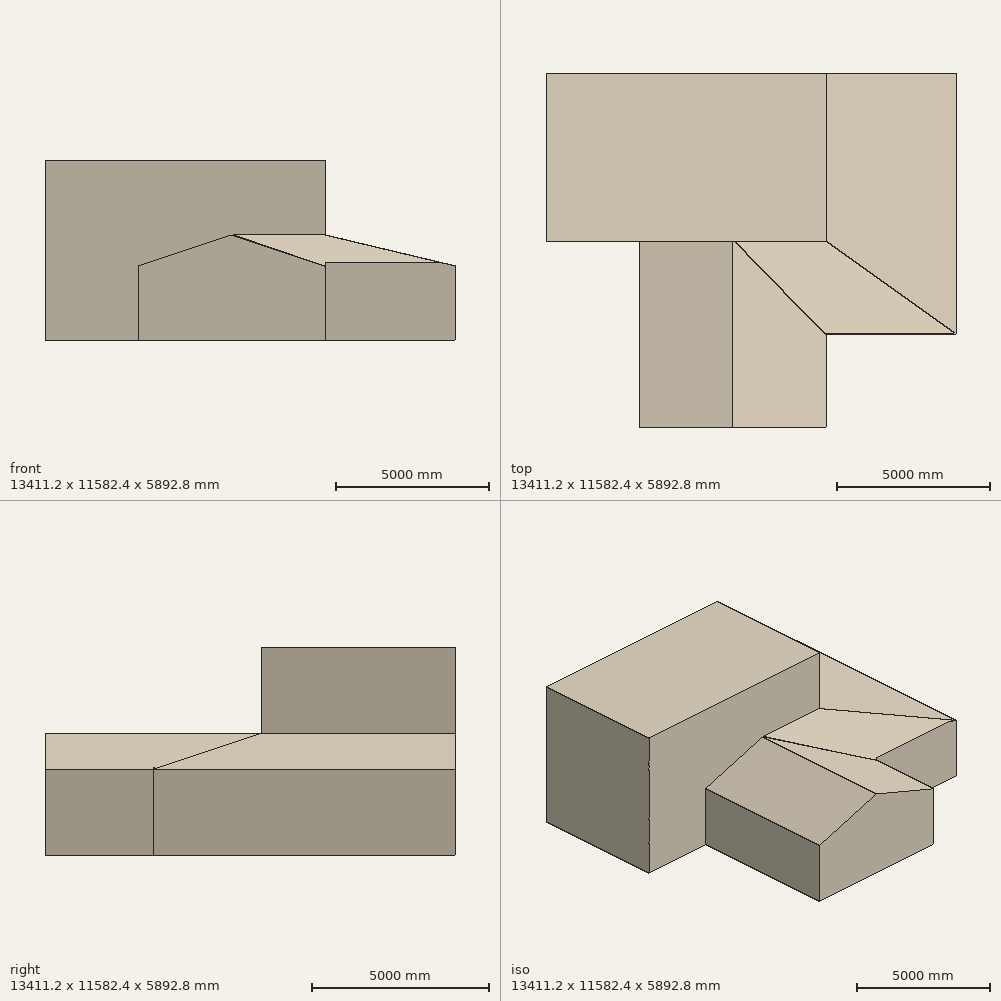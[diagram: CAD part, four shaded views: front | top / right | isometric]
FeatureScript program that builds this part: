
annotation { "Feature Type Name" : "Feature", "Feature Type Description" : "" }
export const myFeature = defineFeature(function(context is Context, id is Id, definition is map)
    precondition{}
    {
        {
            var Q0;
            Q0=qCreatedBy(makeId("Top.planeOp"),FACE);
            var sketch = newSketch(context, id + "F0", { "sketchPlane" : qUnion([Q0])});
            skLineSegment(sketch, "E0.bottom", {"start": v(0, 0) * mm, "end": v(4267.2, 0) * mm});
            skLineSegment(sketch, "E0.top", {"start": v(0, 8534.4) * mm, "end": v(4267.2, 8534.4) * mm});
            skLineSegment(sketch, "E0.left", {"start": v(0, 0) * mm, "end": v(0, 8534.4) * mm});
            skLineSegment(sketch, "E0.right", {"start": v(4267.2, 0) * mm, "end": v(4267.2, 8534.4) * mm});
            skSolve(sketch);
        }
        {
            var Q0;
            Q0=makeQuery(id+"F0.imprint","IMPRINT",FACE,{"disambiguationData":[TD([[makeQuery(id+"F0.imprint","IMPRINT",EDGE,{"derivedFrom":sQuery(id+"F0.wireOp",EDGE,"E0.bottom")}),1.0]])]});
            extrude(context, id + "F1", {"entities" : qUnion([Q0]), "depth" : 3454.4 * mm});
        }
        {
            var Q0;
            Q0=makeQuery(id+"F1.opExtrude","SWEPT_FACE",FACE,{"disambiguationData":[OSD([sQuery(id+"F0.wireOp",EDGE,"E0.bottom")])]});
            var sketch = newSketch(context, id + "F2", { "sketchPlane" : qUnion([Q0])});
            skLineSegment(sketch, "E1.0", {"start": v(0, 2438.4) * mm, "end": v(4267.2, 2438.4) * mm});
            skLineSegment(sketch, "E2", {"start": v(4267.2, 2438.4) * mm, "end": v(0, 3454.4) * mm});
            skSolve(sketch);
        }
        {
            var Q0;
            {var subQ0=sQuery(id+"F2.wireOp",EDGE,"E2");Q0=makeQuery(id+"F2.imprint","IMPRINT",FACE,{"disambiguationData":[TD([[makeQuery(id+"F2.imprint","IMPRINT",EDGE,{"derivedFrom":subQ0}),-1.0]])]});}
            extrude(context, id + "F3", {"entities" : qUnion([Q0]), "operationType" : NewBodyOperationType.REMOVE, "oppositeDirection" : true, "depth" : 12247.14 * mm});
        }
        {
            var Q0;
            Q0=makeQuery(id+"F1.opExtrude","SWEPT_FACE",FACE,{"disambiguationData":[OSD([sQuery(id+"F0.wireOp",EDGE,"E0.left")])]});
            var sketch = newSketch(context, id + "F4", { "sketchPlane" : qUnion([Q0])});
            skLineSegment(sketch, "E3.0", {"start": v(-3048, 3454.4) * mm, "end": v(-3048, 0) * mm});
            skLineSegment(sketch, "E4", {"start": v(-3048, 3454.4) * mm, "end": v(-8534.4, 3454.4) * mm});
            skLineSegment(sketch, "E5", {"start": v(-8534.4, 3454.4) * mm, "end": v(-8534.4, 0) * mm});
            skLineSegment(sketch, "E6", {"start": v(-8534.4, 0) * mm, "end": v(-3048, 0) * mm});
            skSolve(sketch);
        }
        {
            var Q0;
            Q0=makeQuery(id+"F4.imprint","IMPRINT",FACE,{"disambiguationData":[TD([[makeQuery(id+"F4.imprint","IMPRINT",EDGE,{"derivedFrom":sQuery(id+"F4.wireOp",EDGE,"E3.0")}),-1.0]])]});
            extrude(context, id + "F5", {"entities" : qUnion([Q0]), "operationType" : NewBodyOperationType.ADD, "depth" : 9144 * mm});
        }
        {
            var Q0;
            Q0=makeQuery(id+"F5.opExtrude","SWEPT_FACE",FACE,{"disambiguationData":[OSD([sQuery(id+"F4.wireOp",EDGE,"E4")])]});
            extrude(context, id + "F6", {"entities" : qUnion([Q0]), "operationType" : NewBodyOperationType.ADD, "depth" : 2438.4 * mm});
        }
        {
            var Q0;
            Q0=makeQuery(id+"F1.opExtrude","SWEPT_FACE",FACE,{"disambiguationData":[OSD([sQuery(id+"F0.wireOp",EDGE,"E0.left")])]});
            var sketch = newSketch(context, id + "F7", { "sketchPlane" : qUnion([Q0])});
            skLineSegment(sketch, "E7.0", {"start": v(0, 2438.4) * mm, "end": v(-3048, 2438.4) * mm});
            skSolve(sketch);
        }
        {
            var Q0;
            {var subQ0=sQuery(id+"F4.wireOp",EDGE,"E3.0");Q0=makeQuery(id+"F6.boolean.opBoolean","MERGE",FACE,{"derivedFrom":[makeQuery(id+"F5.opExtrude","SWEPT_FACE",FACE,{"disambiguationData":[OSD([subQ0])]}),makeQuery(id+"F6.opExtrude","SWEPT_FACE",FACE,{"disambiguationData":[OSD([sQuery(id+"F0.wireOp",EDGE,"E0.bottom"),sQuery(id+"F0.wireOp",EDGE,"E0.left"),sQuery(id+"F2.wireOp",EDGE,"E2"),subQ0,sQuery(id+"F4.wireOp",EDGE,"E4")])]})]});}
            var sketch = newSketch(context, id + "F8", { "sketchPlane" : qUnion([Q0])});
            skLineSegment(sketch, "E8.0", {"start": v(-6096, 3454.4) * mm, "end": v(-6096, 0) * mm});
            skLineSegment(sketch, "E9.0", {"start": v(-6096, 3454.4) * mm, "end": v(0, 3454.4) * mm});
            skSolve(sketch);
        }
        {
            var Q0;
            Q0 = qSketchRegion(id + "F8", true);
            var Q1;
            {var subQ0=sQuery(id+"F8.wireOp",EDGE,"E8.0");Q1=makeQuery(id+"F8.imprint","IMPRINT",FACE,{"disambiguationData":[TD([[makeQuery(id+"F8.imprint","IMPRINT",EDGE,{"derivedFrom":subQ0}),1.0]])]});}
            extrude(context, id + "F9", {"entities" : qUnion([Q0, Q1]), "operationType" : NewBodyOperationType.ADD, "depth" : 6096 * mm});
        }
        {
            var Q0;
            Q0=makeQuery(id+"F9.opExtrude","CAP_FACE",FACE,{"disambiguationData":[OSD([sQuery(id+"F0.wireOp",EDGE,"E0.left"),sQuery(id+"F4.wireOp",EDGE,"E3.0"),sQuery(id+"F4.wireOp",EDGE,"E6"),sQuery(id+"F8.wireOp",EDGE,"E8.0"),sQuery(id+"F8.wireOp",EDGE,"E9.0")])],"isStart":false});
            var sketch = newSketch(context, id + "F10", { "sketchPlane" : qUnion([Q0])});
            skLineSegment(sketch, "E10.0", {"start": v(-6096, 2438.4) * mm, "end": v(0, 2438.4) * mm});
            skLineSegment(sketch, "E11", {"start": v(-6096, 2438.4) * mm, "end": v(-3048, 3454.4) * mm});
            skSolve(sketch);
        }
        {
            var Q0;
            {var subQ0=sQuery(id+"F10.wireOp",EDGE,"E11");Q0=makeQuery(id+"F10.imprint","IMPRINT",FACE,{"disambiguationData":[TD([[makeQuery(id+"F10.imprint","IMPRINT",EDGE,{"derivedFrom":subQ0}),1.0]])]});}
            extrude(context, id + "F11", {"entities" : qUnion([Q0]), "operationType" : NewBodyOperationType.REMOVE, "oppositeDirection" : true, "depth" : 6096 * mm});
        }
        {
            var Q0;
            Q0=makeQuery(id+"F9.opExtrude","CAP_FACE",FACE,{"disambiguationData":[OSD([sQuery(id+"F0.wireOp",EDGE,"E0.left"),sQuery(id+"F4.wireOp",EDGE,"E3.0"),sQuery(id+"F4.wireOp",EDGE,"E6"),sQuery(id+"F8.wireOp",EDGE,"E8.0"),sQuery(id+"F8.wireOp",EDGE,"E9.0")])],"isStart":false});
            var sketch = newSketch(context, id + "F12", { "sketchPlane" : qUnion([Q0])});
            skLineSegment(sketch, "E12", {"start": v(-3048, 3454.4) * mm, "end": v(0, 2438.4) * mm});
            skLineSegment(sketch, "E13", {"start": v(0, 2438.4) * mm, "end": v(0, 3454.4) * mm});
            skLineSegment(sketch, "E14", {"start": v(0, 3454.4) * mm, "end": v(-3048, 3454.4) * mm});
            skSolve(sketch);
        }
        {
            var Q0;
            Q0=makeQuery(id+"F12.imprint","IMPRINT",FACE,{"disambiguationData":[TD([[makeQuery(id+"F12.imprint","IMPRINT",EDGE,{"derivedFrom":sQuery(id+"F12.wireOp",EDGE,"E12")}),1.0]])]});
            extrude(context, id + "F13", {"entities" : qUnion([Q0]), "operationType" : NewBodyOperationType.REMOVE, "oppositeDirection" : true, "depth" : 6096 * mm});
        }
        {
            var Q0;
            {var subQ0=sQuery(id+"F10.wireOp",EDGE,"E11");Q0=makeQuery(id+"F13.boolean.opBoolean","MERGE",VERTEX,{"derivedFrom":[makeQuery(id+"F11.boolean.opBoolean","COPY",VERTEX,{"derivedFrom":makeQuery(id+"F11.opExtrude","CAP_VERTEX",VERTEX,{"disambiguationData":[OSD([sQuery(id+"F8.wireOp",EDGE,"E9.0"),subQ0])],"isStart":false})}),makeQuery(id+"F13.opExtrude","CAP_VERTEX",VERTEX,{"disambiguationData":[OSD([subQ0,sQuery(id+"F12.wireOp",EDGE,"E12"),sQuery(id+"F12.wireOp",EDGE,"E14")])],"isStart":false})]});}
            var Q1;
            {var subQ0=sQuery(id+"F4.wireOp",EDGE,"E4");var subQ1=sQuery(id+"F4.wireOp",EDGE,"E3.0");var subQ2=sQuery(id+"F2.wireOp",EDGE,"E2");var subQ3=sQuery(id+"F0.wireOp",EDGE,"E0.left");var subQ4=sQuery(id+"F0.wireOp",EDGE,"E0.bottom");var subQ5=makeQuery(id+"F5.opExtrude","CAP_VERTEX",VERTEX,{"disambiguationData":[OSD([subQ4,subQ3,subQ2,subQ1,subQ0])],"isStart":true});Q1=makeQuery(id+"F13.boolean.opBoolean","MERGE",VERTEX,{"derivedFrom":[makeQuery(id+"F9.boolean.opBoolean","MERGE",VERTEX,{"derivedFrom":[makeQuery(id+"F6.boolean.opBoolean","MERGE",VERTEX,{"derivedFrom":[subQ5,makeQuery(id+"F6.opExtrude","CAP_VERTEX",VERTEX,{"disambiguationData":[OSD([subQ4,subQ3,subQ2,subQ1,subQ0]),TDD([subQ5])],"isStart":true})]}),makeQuery(id+"F9.opExtrude","CAP_VERTEX",VERTEX,{"disambiguationData":[OSD([subQ4,subQ3,subQ2,subQ1,subQ0,sQuery(id+"F8.wireOp",EDGE,"E9.0")])],"isStart":true})]}),makeQuery(id+"F13.opExtrude","CAP_VERTEX",VERTEX,{"disambiguationData":[OSD([sQuery(id+"F12.wireOp",EDGE,"E13"),sQuery(id+"F12.wireOp",EDGE,"E14")])],"isStart":false})]});}
            var Q2;
            Q2=sQuery(id+"F7.wireOp",VERTEX,"E7.0.start");
            cPlane(context, id + "F14", {"entities" : qUnion([Q0, Q1, Q2]), "cplaneType" : CPlaneType.THREE_POINT, "offset" : 25.4 * mm, "width" : 152.4 * mm, "height" : 152.4 * mm});
        }
        {
            var Q0;
            Q0=qCreatedBy(id+"F14.planeOp",FACE);
            var sketch = newSketch(context, id + "F15", { "sketchPlane" : qUnion([Q0])});
            skLineSegment(sketch, "E15", {"start": v(0, 743.25) * mm, "end": v(0, 3988.12) * mm});
            skLineSegment(sketch, "E16", {"start": v(0, 3988.12) * mm, "end": v(-2998.1, 3988.12) * mm});
            skLineSegment(sketch, "E17", {"start": v(-2998.1, 3988.12) * mm, "end": v(0, 743.25) * mm});
            skSolve(sketch);
        }
        {
            var Q0;
            Q0=makeQuery(id+"F15.imprint","IMPRINT",FACE,{"disambiguationData":[TD([[makeQuery(id+"F15.imprint","IMPRINT",EDGE,{"derivedFrom":sQuery(id+"F15.wireOp",EDGE,"E15")}),1.0]])]});
            extrude(context, id + "F16", {"entities" : qUnion([Q0]), "operationType" : NewBodyOperationType.ADD, "oppositeDirection" : true, "depth" : 25.4 * mm});
        }
        {
            var Q0;
            Q0=qCreatedBy(id+"F14.planeOp",FACE);
            var sketch = newSketch(context, id + "F17", { "sketchPlane" : qUnion([Q0])});
            skLineSegment(sketch, "E18", {"start": v(0, 807.77) * mm, "end": v(4260.71, 807.77) * mm});
            skLineSegment(sketch, "E19", {"start": v(4260.71, 807.77) * mm, "end": v(0, 3984.47) * mm});
            skLineSegment(sketch, "E20", {"start": v(0, 3984.47) * mm, "end": v(0, 807.77) * mm});
            skSolve(sketch);
        }
        {
            var Q0;
            Q0 = qSketchRegion(id + "F17", true);
            extrude(context, id + "F18", {"entities" : qUnion([Q0]), "operationType" : NewBodyOperationType.REMOVE, "depth" : 3511.2 * mm});
        }
    });
